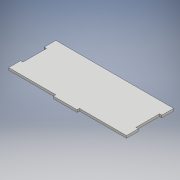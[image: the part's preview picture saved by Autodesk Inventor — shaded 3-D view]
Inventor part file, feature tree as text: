
AUTODESK INVENTOR PART (.ipt)
format: ipt  version: 2017 (Build 210142000, 142)  size: 114,688 bytes
history: native  units: mm
features: extrude x1, sketch x1
ambient origin geometry x8: Origin, YZ Plane, XZ Plane, XY Plane, X Axis, Y Axis, Z Axis, Center Point
bodies: Solid1 (feature_tree)
feature tree (2):
  extrude  "Extrusion1"  Depth=30.0mm
  sketch  "Sketch1"  dims[d1=150.0mm d2=60.0mm d6=3.0mm d7=15.0mm d8=3.0mm d10=30.0mm d11=30.0mm d12=3.0mm d13=3.0mm d14=15.0mm d15=3.0mm d16=0.0mm]
